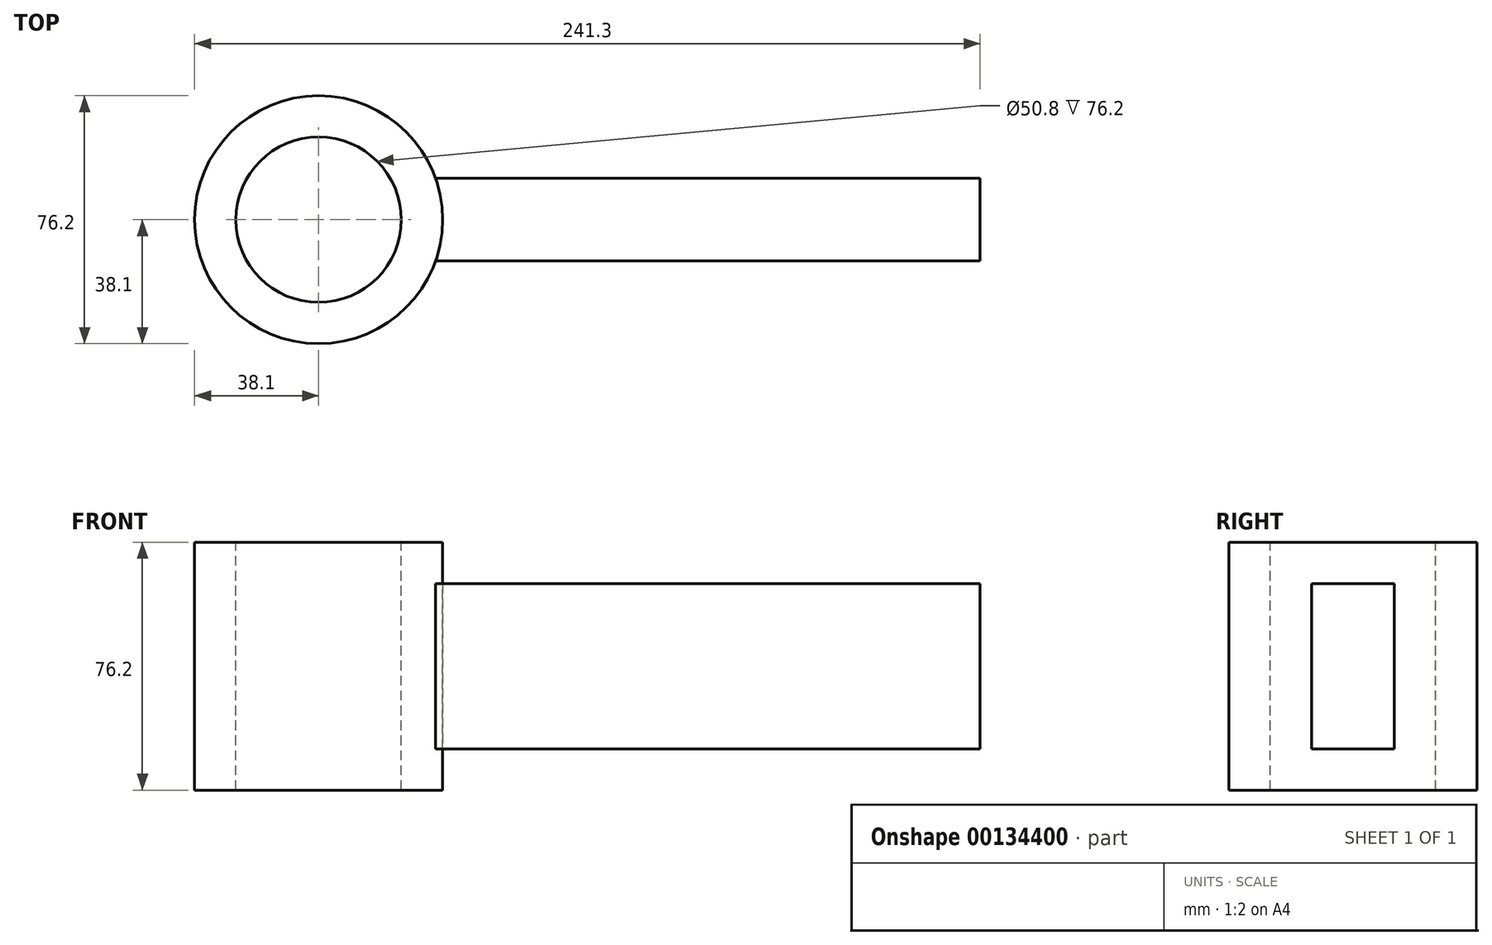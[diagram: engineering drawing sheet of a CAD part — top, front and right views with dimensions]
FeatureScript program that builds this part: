
annotation { "Feature Type Name" : "Feature", "Feature Type Description" : "" }
export const myFeature = defineFeature(function(context is Context, id is Id, definition is map)
    precondition{}
    {
        {
            var Q0;
            Q0=qCreatedBy(makeId("Top.planeOp"),FACE);
            var sketch = newSketch(context, id + "F0", { "sketchPlane" : qUnion([Q0])});
            skCircle(sketch, "E0", {"center": v(0, 0) * mm, "radius": 38.1 * mm});
            skCircle(sketch, "E1", {"center": v(0, 0) * mm, "radius": 25.4 * mm});
            skLineSegment(sketch, "E2", {"start": v(0, 0) * mm, "end": v(203.2, 0) * mm, "construction": true});
            skLineSegment(sketch, "E3", {"start": v(203.2, -12.7) * mm, "end": v(203.2, 12.7) * mm});
            skLineSegment(sketch, "E4", {"start": v(203.2, 12.7) * mm, "end": v(35.92, 12.7) * mm});
            skLineSegment(sketch, "E5", {"start": v(203.2, -12.7) * mm, "end": v(35.92, -12.7) * mm});
            skPoint(sketch, "E6.orphan", {"position": v(0, -12.7) * mm});
            skSolve(sketch);
        }
        {
            var Q0;
            Q0=makeQuery(id+"F0.imprint","IMPRINT",FACE,{"disambiguationData":[TD([[makeQuery(id+"F0.imprint","IMPRINT",EDGE,{"derivedFrom":sQuery(id+"F0.wireOp",EDGE,"E1")}),-1.0]])]});
            extrude(context, id + "F1", {"entities" : qUnion([Q0]), "endBound" : BoundingType.SYMMETRIC, "oppositeDirection" : true, "depth" : 76.2 * mm});
        }
        {
            var Q0;
            Q0=makeQuery(id+"F0.imprint","IMPRINT",FACE,{"disambiguationData":[TD([[makeQuery(id+"F0.imprint","IMPRINT",EDGE,{"derivedFrom":sQuery(id+"F0.wireOp",EDGE,"E3")}),1.0]])]});
            var Q1;
            Q1=sQuery(id+"F0.wireOp",EDGE,"E4");
            var Q2;
            Q2=sQuery(id+"F0.wireOp",EDGE,"E5");
            var Q3;
            Q3=sQuery(id+"F0.wireOp",EDGE,"E3");
            var Q4;
            Q4=sQuery(id+"F0.wireOp",EDGE,"KCf2Kyap-OC3a-F185-X5UD-6drBQppEpbKy");
            extrude(context, id + "F2", {"entities" : qUnion([Q0]), "surfaceEntities" : qUnion([Q1, Q2, Q3, Q4]), "endBound" : BoundingType.SYMMETRIC, "depth" : 50.8 * mm});
        }
    });
